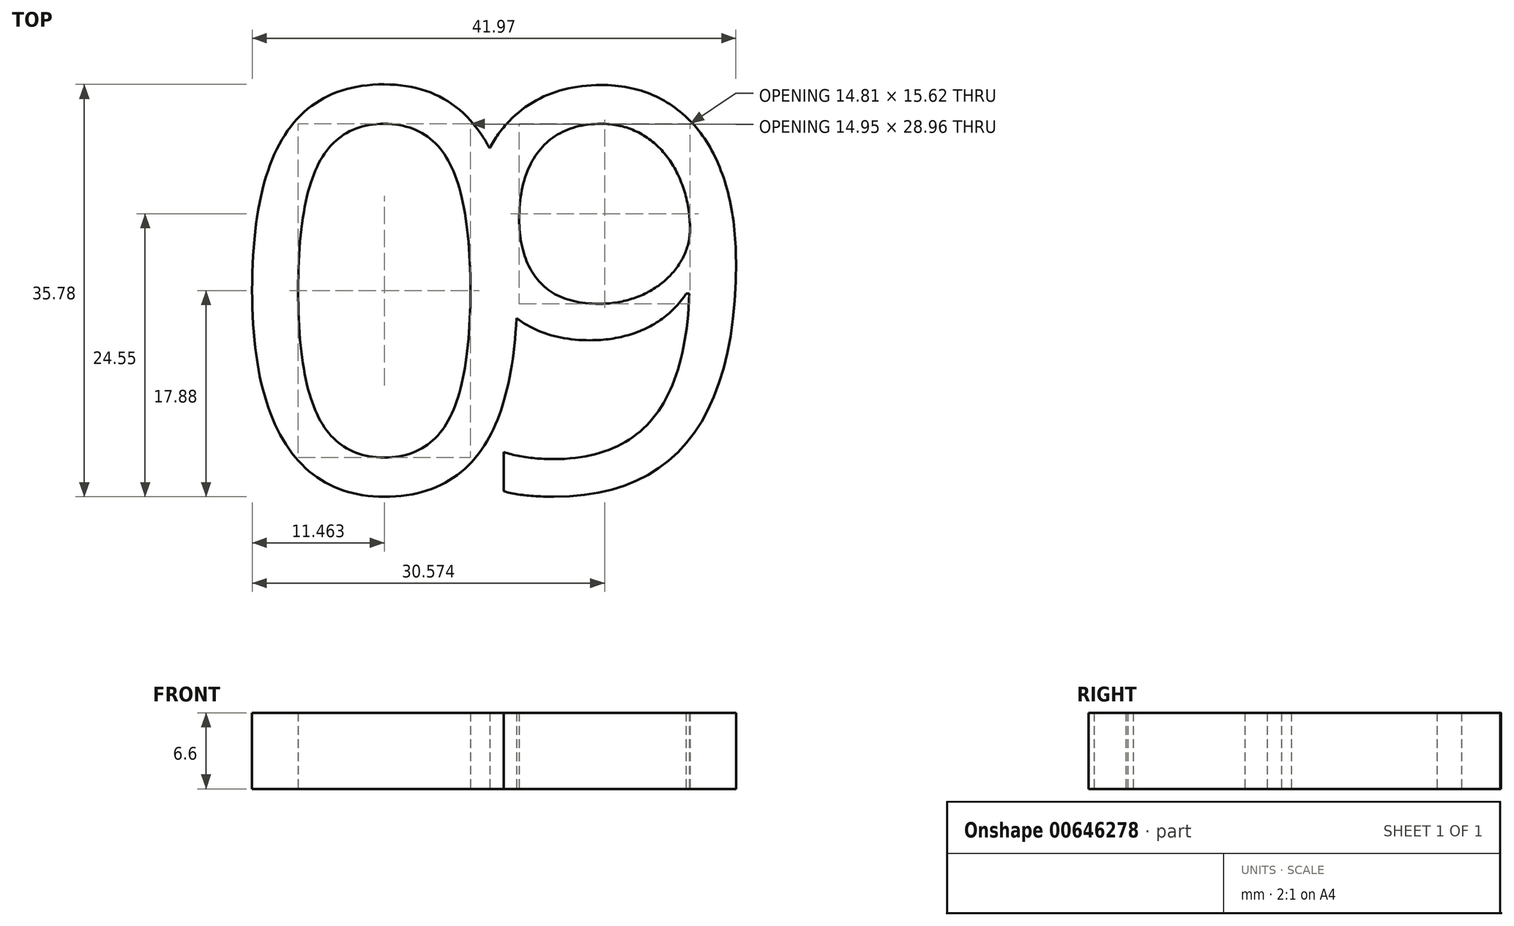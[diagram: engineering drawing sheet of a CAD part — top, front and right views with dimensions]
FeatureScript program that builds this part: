
annotation { "Feature Type Name" : "Feature", "Feature Type Description" : "" }
export const myFeature = defineFeature(function(context is Context, id is Id, definition is map)
    precondition{}
    {
        {
            var Q0;
            Q0=qCreatedBy(makeId("Top.planeOp"),FACE);
            var sketch = newSketch(context, id + "F0", { "sketchPlane" : qUnion([Q0])});
            skText(sketch, "E0", { "text": "0", "fontName": "OpenSans-Regular.ttf"});
            skText(sketch, "E1", { "text": "9", "fontName": "OpenSans-Regular.ttf"});
            const initialGuessF0  = {"E0": [-0.03067, -0.01255, 1, 0, 0.03505], "E1": [-0.01149, -0.01255, 1, 0, 0.03505]};
            skSetInitialGuess(sketch, initialGuessF0);
            skSolve(sketch);
        }
        {
            var Q0;
            Q0 = qSketchRegion(id + "F0", true);
            extrude(context, id + "F1", {"entities" : qUnion([Q0]), "depth" : 6.6 * mm, "offsetDistance" : 25 * mm});
        }
    });
